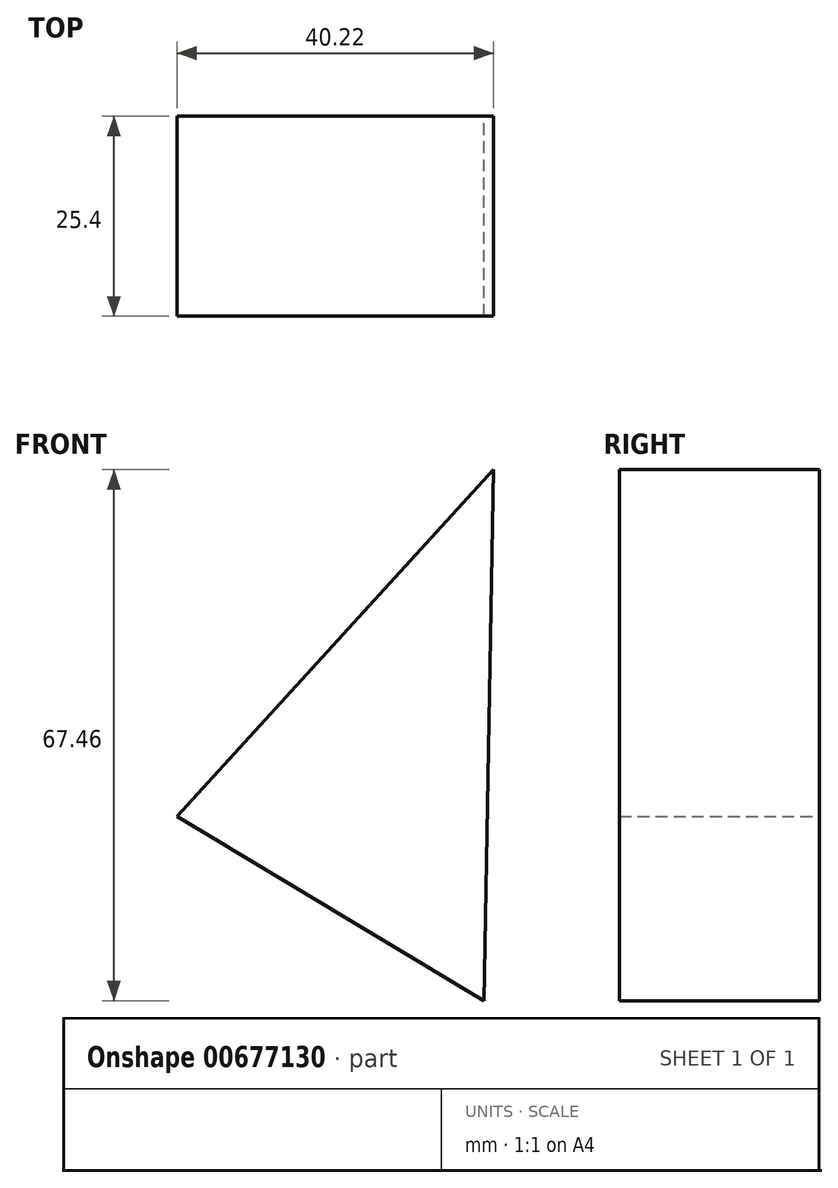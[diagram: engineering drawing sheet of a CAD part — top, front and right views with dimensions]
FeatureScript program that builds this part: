
annotation { "Feature Type Name" : "Feature", "Feature Type Description" : "" }
export const myFeature = defineFeature(function(context is Context, id is Id, definition is map)
    precondition{}
    {
        {
            var Q0;
            Q0=qCreatedBy(makeId("Front.planeOp"),FACE);
            var sketch = newSketch(context, id + "F0", { "sketchPlane" : qUnion([Q0])});
            skLineSegment(sketch, "E0", {"start": v(0, 0) * mm, "end": v(40.22, 44.07) * mm});
            skLineSegment(sketch, "E1", {"start": v(40.22, 44.07) * mm, "end": v(39, -23.4) * mm});
            skLineSegment(sketch, "E2", {"start": v(39, -23.4) * mm, "end": v(0, 0) * mm});
            skSolve(sketch);
        }
        {
            var Q0;
            Q0 = qSketchRegion(id + "F0", true);
            extrude(context, id + "F1", {"entities" : qUnion([Q0]), "depth" : 25.4 * mm, "offsetDistance" : 25.4 * mm});
        }
    });
